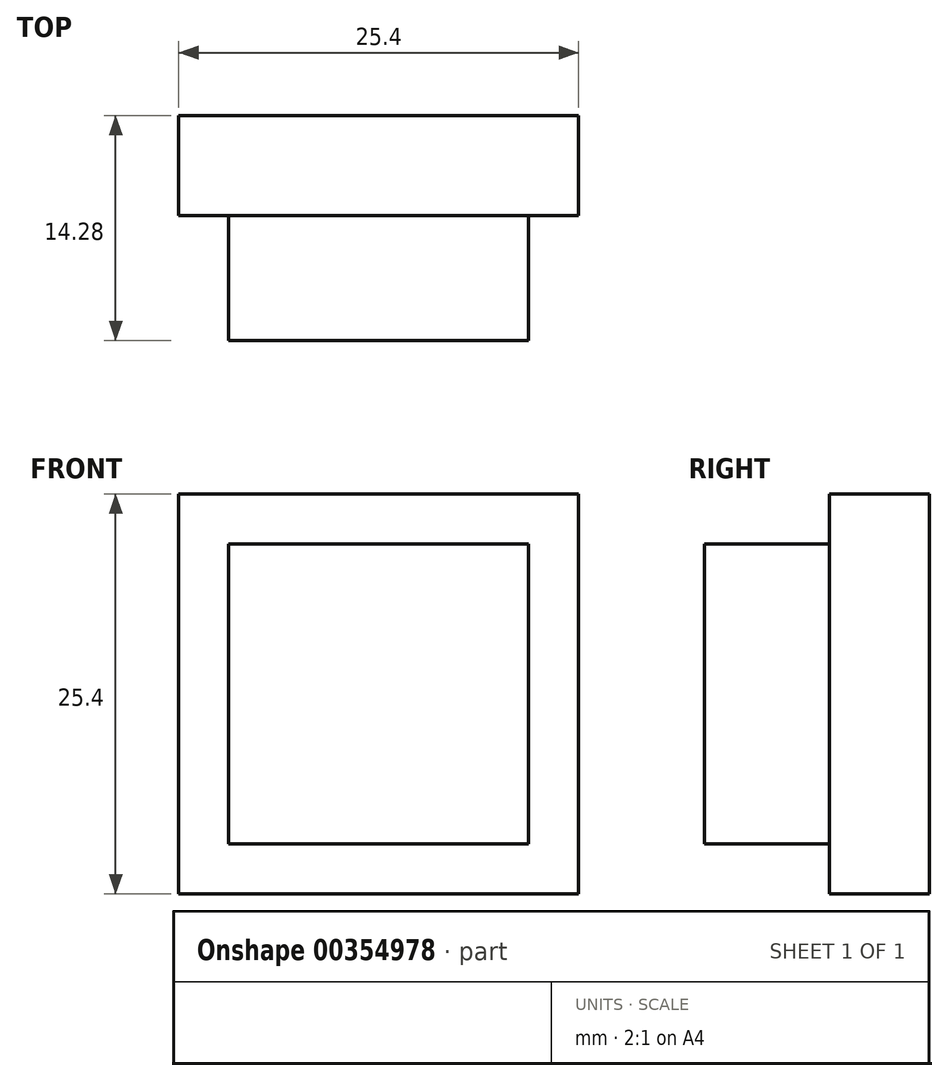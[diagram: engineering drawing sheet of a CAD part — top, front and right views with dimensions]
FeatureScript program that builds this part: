
annotation { "Feature Type Name" : "Feature", "Feature Type Description" : "" }
export const myFeature = defineFeature(function(context is Context, id is Id, definition is map)
    precondition{}
    {
        {
            var Q0;
            Q0=qCreatedBy(makeId("Front.planeOp"),FACE);
            var sketch = newSketch(context, id + "F0", { "sketchPlane" : qUnion([Q0])});
            skLineSegment(sketch, "E0.bottom", {"start": v(12.7, -12.7) * mm, "end": v(-12.7, -12.7) * mm});
            skLineSegment(sketch, "E0.top", {"start": v(12.7, 12.7) * mm, "end": v(-12.7, 12.7) * mm});
            skLineSegment(sketch, "E0.left", {"start": v(12.7, -12.7) * mm, "end": v(12.7, 12.7) * mm});
            skLineSegment(sketch, "E0.right", {"start": v(-12.7, -12.7) * mm, "end": v(-12.7, 12.7) * mm});
            skPoint(sketch, "E0.middle", {"position": v(0, 0) * mm});
            skLineSegment(sketch, "E1.bottom", {"start": v(9.53, -9.52) * mm, "end": v(-9.52, -9.53) * mm});
            skLineSegment(sketch, "E1.top", {"start": v(9.52, 9.53) * mm, "end": v(-9.53, 9.53) * mm});
            skLineSegment(sketch, "E1.left", {"start": v(9.53, -9.52) * mm, "end": v(9.52, 9.53) * mm});
            skLineSegment(sketch, "E1.right", {"start": v(-9.52, -9.53) * mm, "end": v(-9.53, 9.52) * mm});
            skSolve(sketch);
        }
        {
            var Q0;
            Q0=makeQuery(id+"F0.imprint","IMPRINT",FACE,{"disambiguationData":[TD([[makeQuery(id+"F0.imprint","IMPRINT",EDGE,{"derivedFrom":sQuery(id+"F0.wireOp",EDGE,"E0.bottom")}),-1.0]])]});
            var sketch = newSketch(context, id + "F1", { "sketchPlane" : qUnion([Q0])});
            skSolve(sketch);
        }
        {
            var Q0;
            Q0=makeQuery(id+"F0.imprint","IMPRINT",FACE,{"disambiguationData":[TD([[makeQuery(id+"F0.imprint","IMPRINT",EDGE,{"derivedFrom":sQuery(id+"F0.wireOp",EDGE,"E0.bottom")}),-1.0]])]});
            extrude(context, id + "F2", {"entities" : qUnion([Q0]), "depth" : 6.35 * mm});
        }
        {
            var Q0;
            Q0=makeQuery(id+"F1.imprint","IMPRINT",FACE,{"disambiguationData":[TD([[makeQuery(id+"F1.imprint","IMPRINT",EDGE,{"derivedFrom":makeQuery(id+"F0.imprint","IMPRINT",EDGE,{"derivedFrom":sQuery(id+"F0.wireOp",EDGE,"E1.bottom")})}),-1.0]])]});
            extrude(context, id + "F3", {"entities" : qUnion([Q0]), "operationType" : NewBodyOperationType.ADD, "depth" : 14.28 * mm});
        }
    });
